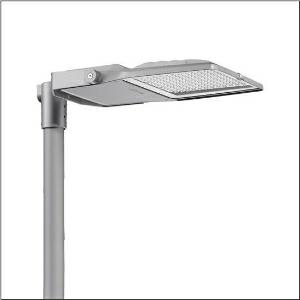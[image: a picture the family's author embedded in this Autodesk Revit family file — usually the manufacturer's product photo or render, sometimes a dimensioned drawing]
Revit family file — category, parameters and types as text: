
# Revit family: floodlight_fl_21_midi___pl52_5xa7786e2d3a_7127
name_source: partatom
category: Lighting Fixtures
units: mm (PartAtom-declared; Revit-internal decimal feet)

## family parameters
Cut with Voids When Loaded = No
Host = Face
Light Source = No
Part Type = Normal
Room Calculation Point = No
Round Connector Dimension = Use Diameter
Shared = No

## types (1)
- --- (1 x LED, 26940 lm, 212.4 W, 3000K)
    Apparent Load = 212 VA
    CIE Flux Codes = 26 60 98 100 100
    Color Rendering = 70
    Color Temperature = 3000K
    Default Elevation = 1800 mm
    Description = Floodlight FL 21 midi, floodlight, primary light control with lens, of PMMA, primary optical cover: protective disc, of toughened safety glass, transparent, light distribution: PL52, light emission: direct distribution, installation type: surface-mounted, LED, High Power LED, rated luminous flux: 26.940lm, luminous efficacy: 127lm/W, light colour: 730, colour temperature: 3000K, control gear: Smart Interface (Zhaga), control: flexible luminous flux parameterisation, time-dependent luminous flux control, constant luminous flux control, overheat protection, pre-setting: logarithmic dimming characteristic, with terminal, 6-pole, mains connection: 220..240V, AC, 50/60Hz, start of lifetime: 212W, end of service life: 231W, reduction: 95W, luminaire housing, of diecast aluminium, powder-coated, Siteco® metallic grey (DB 702S), corrosivity category C5 mid according to DIN EN ISO 12944, suitable for swimming pools, chlorine-resistant, sealing non-destructively replaceable, please order mast flange separately, mast bracket, of steel, galvanised, powder-coated, Siteco® metallic grey (DB 702S), Smart Interface below and above, protection rating (complete): IP66, insulation class (complete): insulation class II (safety insulation), certification: CE, ENEC, VDE, protection symbol: D, impact resistance: IK08, permissible operating ambient temperature: -40..+40°C, permissible operating ambient temperature for outdoor applications: -40..+50°C, standard: DIN EN 12944, LABS conformity tested according to VDMA 24364:2018-05, packaging unit: 1 piece

Light Distribution: PL52
    Height = 76 mm
    Lamp = 1 x LED
    Lamp Light Flux = 26940 lm
    Lamp Power = 212.4 W
    Lamp count = 1
    Length = 657 mm
    Luminous efficacy = 127 lm/W
    Manufacturer = Siteco
    ModVariant = No
    Model = 5XA7786E2D3A
    Number of Poles = 1
    OnlyDefault = Yes
    Power Factor = 1
    Product Name = Floodlight FL 21 midi | PL52
    Product group = floodlight | pylon annexe
    ProductGroupID = 6200
    Protection Class = Protection class II
    Protection Degree = IP 66
    RLX_Detail_Level = 1
    RLX_Emergency_Light_Flux = 0 lm
    RLX_Emergency_Type = 0
    RLX_Emergency_Type_DB = No
    RlxData = <blob elided: 153637 chars, md5=f6d639e0>
    Socket = socket
    Standby Power = 0 W
    System Light Flux = 26940 lm
    System Power = 212 W
    Type Comments = factory setting: luminous flux: 100 % | dim-lin: 254 | 710 mA
    Type Image = l_1007123.jpg
    URL = http://relux.com
    VarID = @adj_177554
    Voltage = 0 V
    Weight = 0.00 kg
    Width = 442 mm

## geometry (parser evidence)
native form markers: Blend x4, Sweep x14
no freeform markers — native parametric forms only
